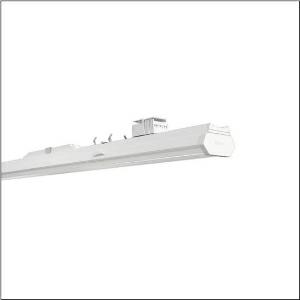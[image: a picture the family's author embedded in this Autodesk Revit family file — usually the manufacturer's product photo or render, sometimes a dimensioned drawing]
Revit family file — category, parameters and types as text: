
# Revit family: licross_r__11_protected_mo_51td11dn495g_7274
name_source: partatom
category: Lighting Fixtures
units: mm (PartAtom-declared; Revit-internal decimal feet)

## family parameters
Cut with Voids When Loaded = No
Host = Face
Light Source = No
Part Type = Normal
Room Calculation Point = No
Round Connector Dimension = Use Diameter
Shared = No

## types (1)
- --- (1 x LED, 9930 lm, 57.1 W, 4000K)
    Apparent Load = 57 VA
    CIE Flux Codes = 83 94 98 100 100
    Color Rendering = 80
    Color Temperature = 4000K
    Default Elevation = 1800 mm
    Description = Licross® 11 Protected MO, luminaire insert, of sheet steel, galvanised, coil coated, white, length: 1.500mm, width: 90mm, height: 101mm, LED rated luminous flux: 9.930lm, light colour: 840, control gear: DALI 2, with plug, 5-pole, with phase selection, mains connection: 220..240V, AC, 50/60Hz, rated input power: 57W, halogen-free wiring, primary light control with lens, of plastic, primary optical cover: cover, of PMMA, light emission: direct distribution, primary light characteristic: symmetric, protection rating (complete): IP54, insulation class (complete): insulation class I (protective earthing), certification: CE, ENEC, VDE, UKCA, protection symbol: D if used in an environment with non-conductive dust loads with corresponding accessories, impact resistance: IK06, permissible ambient temperature for indoor applications: -25..+35°C, corresponds to IFS (International Featured Standards) requirements for safety and quality in the food industry, reducing of maximum allowable ambient temperature of 5°C with ceiling mounting, LABS conformity tested according to VDMA 24364:2018-05, packaging unit: 1 piece
    Height = 92 mm
    Lamp = 1 x LED
    Lamp Light Flux = 9930 lm
    Lamp Power = 57.1 W
    Lamp count = 1
    Length = 1500 mm
    Luminous efficacy = 174 lm/W
    Manufacturer = Siteco
    ModVariant = No
    Model = 51TD11DN495G
    Mounting Place = Ceiling
    Mounting Type = Pendant
    Number of Poles = 1
    OnlyDefault = Yes
    Power Factor = 1
    Product Name = Licross® 11 Protected MO
    Product group = luminaire insert
    ProductGroupID = 902
    Protection Class = Protection class I
    Protection Degree = IP 54
    RLX_Detail_Level = 1
    RLX_Emergency_Light_Flux = 0 lm
    RLX_Emergency_Type = 0
    RLX_Emergency_Type_DB = No
    RlxData = <blob elided: 24133 chars, md5=6b3ffa0a>
    Socket = socket
    Standby Power = 0 W
    System Light Flux = 9930 lm
    System Power = 57 W
    Type Comments = factory setting: luminous flux: 100 % | dim-lin: 254 | 378 mA
    Type Image = l_1256145.jpg
    URL = http://relux.com
    VarID = @adj_101014
    Voltage = 0 V
    Weight = 0.00 kg
    Width = 88 mm

## geometry (parser evidence)
native form markers: Blend x4, Sweep x10
no freeform markers — native parametric forms only
